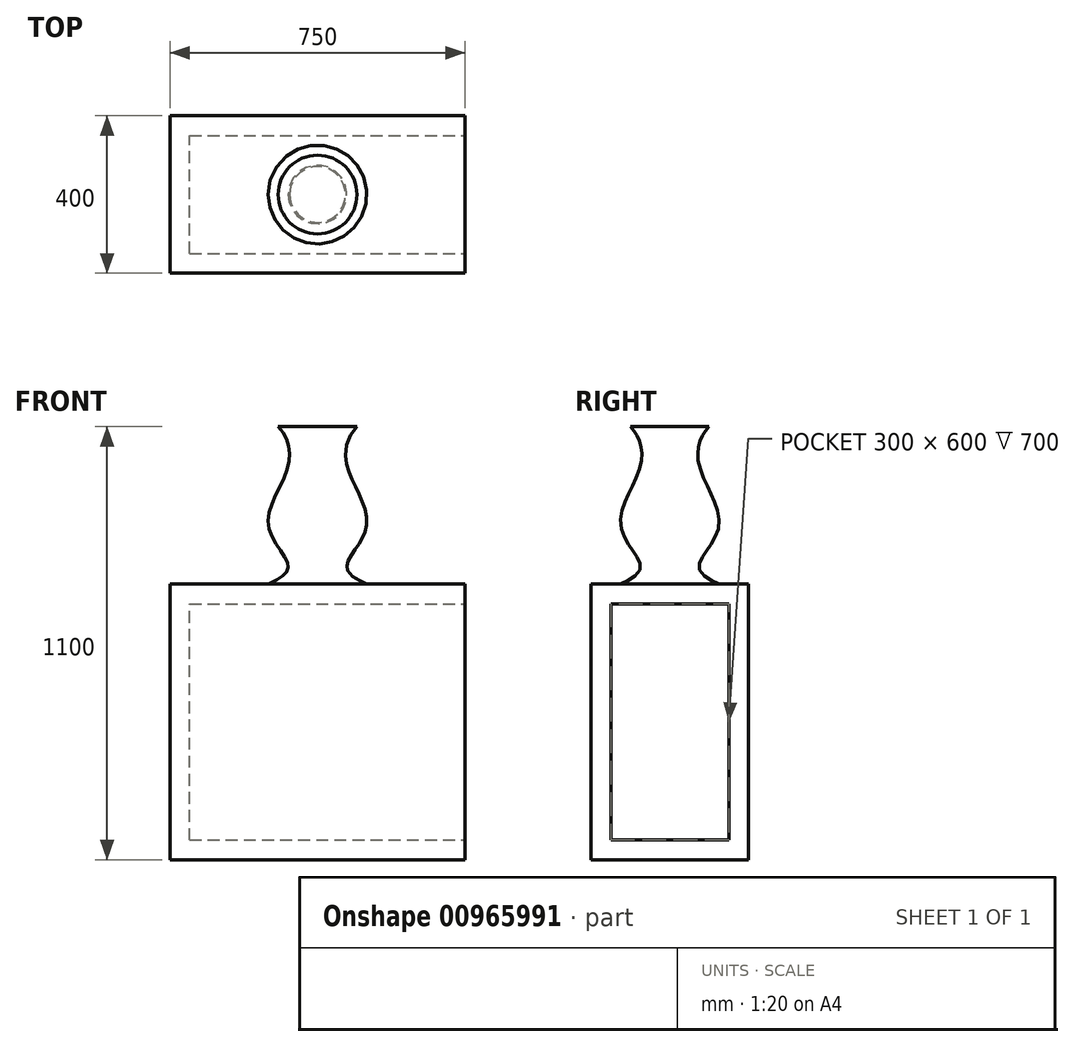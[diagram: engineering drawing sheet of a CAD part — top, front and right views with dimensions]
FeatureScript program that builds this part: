
annotation { "Feature Type Name" : "Feature", "Feature Type Description" : "" }
export const myFeature = defineFeature(function(context is Context, id is Id, definition is map)
    precondition{}
    {
        {
            var Q0;
            Q0=qCreatedBy(makeId("Top.planeOp"),FACE);
            var sketch = newSketch(context, id + "F0", { "sketchPlane" : qUnion([Q0])});
            skLineSegment(sketch, "E0.bottom", {"start": v(-375, 200) * mm, "end": v(375, 200) * mm});
            skLineSegment(sketch, "E0.top", {"start": v(-375, -200) * mm, "end": v(375, -200) * mm});
            skLineSegment(sketch, "E0.left", {"start": v(-375, 200) * mm, "end": v(-375, -200) * mm});
            skLineSegment(sketch, "E0.right", {"start": v(375, 200) * mm, "end": v(375, -200) * mm});
            skLineSegment(sketch, "E1", {"start": v(-375, 200) * mm, "end": v(375, -200) * mm, "construction": true});
            skSolve(sketch);
        }
        {
            var Q0;
            Q0 = qSketchRegion(id + "F0", true);
            extrude(context, id + "F1", {"entities" : qUnion([Q0]), "depth" : 700 * mm, "offsetDistance" : 25 * mm});
        }
        {
            var Q0;
            Q0=makeQuery(id+"F1.opExtrude","SWEPT_FACE",FACE,{"disambiguationData":[OSD([sQuery(id+"F0.wireOp",EDGE,"E0.right")])]});
            var sketch = newSketch(context, id + "F2", { "sketchPlane" : qUnion([Q0])});
            skLineSegment(sketch, "E2.0", {"start": v(-150, 650) * mm, "end": v(-150, 50) * mm});
            skLineSegment(sketch, "E2.1", {"start": v(150, 650) * mm, "end": v(-150, 650) * mm});
            skLineSegment(sketch, "E2.2", {"start": v(150, 650) * mm, "end": v(150, 50) * mm});
            skLineSegment(sketch, "E2.3", {"start": v(150, 50) * mm, "end": v(-150, 50) * mm});
            skSolve(sketch);
        }
        {
            var Q0;
            Q0 = qSketchRegion(id + "F2", true);
            var Q1;
            Q1=makeQuery(id+"F1.opExtrude","SWEPT_FACE",FACE,{"disambiguationData":[OSD([sQuery(id+"F0.wireOp",EDGE,"E0.left")])]});
            extrude(context, id + "F3", {"entities" : qUnion([Q0]), "operationType" : NewBodyOperationType.REMOVE, "endBound" : BoundingType.UP_TO_SURFACE, "oppositeDirection" : true, "depth" : 25 * mm, "endBoundEntityFace" : qUnion([Q1]), "hasOffset" : true, "offsetDistance" : 50 * mm});
        }
        {
            var Q0;
            Q0=qCreatedBy(makeId("Front.planeOp"),FACE);
            var sketch = newSketch(context, id + "F4", { "sketchPlane" : qUnion([Q0])});
            skFitSpline(sketch, "E3", {"points": [v(-100, 1100) * mm, v(-75, 1000) * mm, v(-125, 850) * mm, v(-75, 750) * mm, v(-125, 700) * mm], "startDerivative": vector(309.02, -314.27) * mm, "endDerivative": vector(-538.87, -240.82) * mm});
            skLineSegment(sketch, "E4", {"start": v(0, 0) * mm, "end": v(0, 1100) * mm, "construction": true});
            skLineSegment(sketch, "E5", {"start": v(-100, 1100) * mm, "end": v(0, 1100) * mm});
            skLineSegment(sketch, "E6", {"start": v(-125, 700) * mm, "end": v(0, 700) * mm});
            skLineSegment(sketch, "E7", {"start": v(0, 700) * mm, "end": v(0, 1100) * mm});
            skSolve(sketch);
        }
        {
            var Q0;
            Q0=makeQuery(id+"F4.imprint","IMPRINT",FACE,{"disambiguationData":[TD([[makeQuery(id+"F4.imprint","IMPRINT",EDGE,{"derivedFrom":sQuery(id+"F4.wireOp",EDGE,"E3")}),1.0]])]});
            var Q1;
            Q1=sQuery(id+"F4.wireOp",EDGE,"E4");
            revolve(context, id + "F5", {"surfaceOperationType" : NewSurfaceOperationType.NEW, "entities" : qUnion([Q0]), "axis" : qUnion([Q1]), "revolveType" : RevolveType.FULL});
        }
    });
